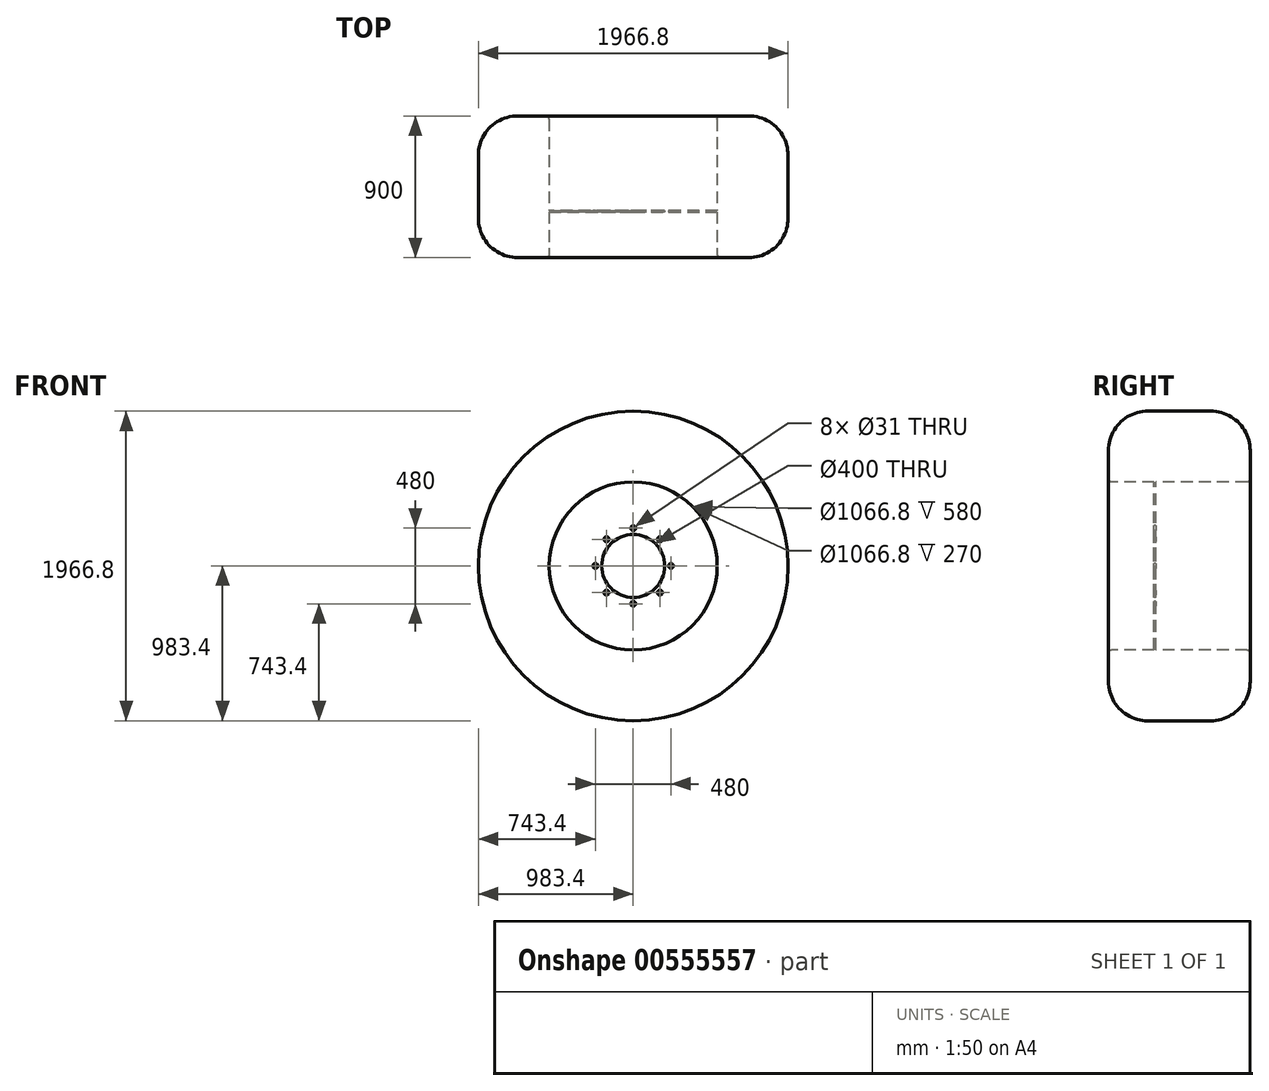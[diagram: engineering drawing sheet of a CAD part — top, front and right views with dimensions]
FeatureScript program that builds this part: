
annotation { "Feature Type Name" : "Feature", "Feature Type Description" : "" }
export const myFeature = defineFeature(function(context is Context, id is Id, definition is map)
    precondition{}
    {
        {
            var Q0;
            Q0=qCreatedBy(makeId("Right.planeOp"),FACE);
            var sketch = newSketch(context, id + "F0", { "sketchPlane" : qUnion([Q0])});
            skLineSegment(sketch, "E0", {"start": v(-3333.33, 0) * mm, "end": v(4000, 0) * mm, "construction": true});
            skLineSegment(sketch, "E1", {"start": v(0, 200) * mm, "end": v(0, 533.4) * mm});
            skLineSegment(sketch, "E2", {"start": v(0, 533.4) * mm, "end": v(-290, 533.4) * mm});
            skLineSegment(sketch, "E3", {"start": v(-290, 533.4) * mm, "end": v(-290, 983.4) * mm});
            skLineSegment(sketch, "E4", {"start": v(-290, 983.4) * mm, "end": v(610, 983.4) * mm});
            skLineSegment(sketch, "E5", {"start": v(610, 983.4) * mm, "end": v(610, 533.4) * mm});
            skLineSegment(sketch, "E6", {"start": v(610, 533.4) * mm, "end": v(10, 533.4) * mm});
            skLineSegment(sketch, "E7", {"start": v(10, 533.4) * mm, "end": v(10, 200) * mm});
            skLineSegment(sketch, "E8", {"start": v(10, 200) * mm, "end": v(0, 200) * mm});
            skSolve(sketch);
        }
        {
            var Q0;
            Q0 = qSketchRegion(id + "F0", true);
            var Q1;
            Q1=sQuery(id+"F0.wireOp",EDGE,"E0");
            revolve(context, id + "F1", {"entities" : qUnion([Q0]), "axis" : qUnion([Q1]), "revolveType" : RevolveType.FULL});
        }
        {
            var Q0;
            Q0=makeQuery(id+"F1.opRevolve","SWEPT_EDGE",EDGE,{"disambiguationData":[OSD([sQuery(id+"F0.wireOp",EDGE,"E3"),sQuery(id+"F0.wireOp",EDGE,"E4")])]});
            var Q1;
            Q1=makeQuery(id+"F1.opRevolve","SWEPT_EDGE",EDGE,{"disambiguationData":[OSD([sQuery(id+"F0.wireOp",EDGE,"E4"),sQuery(id+"F0.wireOp",EDGE,"E5")])]});
            fillet(context, id + "F2", {"entities" : qUnion([Q0, Q1]), "tangentPropagation" : true, "radius" : 250 * mm, "defaultsChanged" : true, "vertexSettings" : [], "allowEdgeOverflow" : false});
        }
        {
            var Q0;
            Q0=makeQuery(id+"F1.opRevolve","SWEPT_EDGE",EDGE,{"disambiguationData":[OSD([sQuery(id+"F0.wireOp",EDGE,"E2"),sQuery(id+"F0.wireOp",EDGE,"E3")])]});
            var Q1;
            Q1=makeQuery(id+"F1.opRevolve","SWEPT_EDGE",EDGE,{"disambiguationData":[OSD([sQuery(id+"F0.wireOp",EDGE,"E5"),sQuery(id+"F0.wireOp",EDGE,"E6")])]});
            fillet(context, id + "F3", {"entities" : qUnion([Q0, Q1]), "tangentPropagation" : true, "radius" : 20 * mm, "defaultsChanged" : true, "vertexSettings" : [], "allowEdgeOverflow" : false});
        }
        {
            var Q0;
            Q0=makeQuery(id+"F1.opRevolve","SWEPT_FACE",FACE,{"disambiguationData":[OSD([sQuery(id+"F0.wireOp",EDGE,"E1")])]});
            var sketch = newSketch(context, id + "F4", { "sketchPlane" : qUnion([Q0])});
            skCircle(sketch, "E9", {"center": v(0, 240) * mm, "radius": 15.5 * mm});
            skCircle(sketch, "E10.1.0", {"center": v(-169.7, 169.7) * mm, "radius": 15.5 * mm});
            skCircle(sketch, "E10.2.0", {"center": v(-240, 0) * mm, "radius": 15.5 * mm});
            skCircle(sketch, "E10.3.0", {"center": v(-169.7, -169.7) * mm, "radius": 15.5 * mm});
            skCircle(sketch, "E10.4.0", {"center": v(0, -240) * mm, "radius": 15.5 * mm});
            skCircle(sketch, "E10.5.0", {"center": v(169.7, -169.7) * mm, "radius": 15.5 * mm});
            skCircle(sketch, "E10.6.0", {"center": v(240, 0) * mm, "radius": 15.5 * mm});
            skCircle(sketch, "E10.7.0", {"center": v(169.7, 169.7) * mm, "radius": 15.5 * mm});
            skPoint(sketch, "E10.center", {"position": v(0, 0) * mm});
            skSolve(sketch);
        }
        {
            var Q0;
            Q0 = qSketchRegion(id + "F4", true);
            extrude(context, id + "F5", {"entities" : qUnion([Q0]), "operationType" : NewBodyOperationType.REMOVE, "oppositeDirection" : true, "depth" : 25 * mm, "offsetDistance" : 25 * mm});
        }
    });
